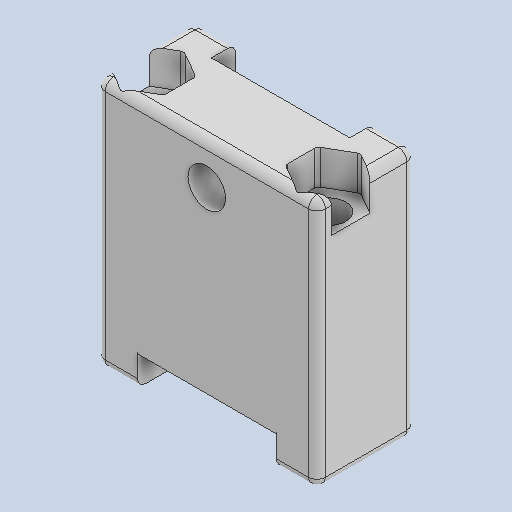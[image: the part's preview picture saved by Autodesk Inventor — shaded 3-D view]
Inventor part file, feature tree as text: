
AUTODESK INVENTOR PART (.ipt)
format: ipt  version: 2022 (Build 260153000, 153)  size: 158,208 bytes
history: native  units: in
note: dims shown in document units (in); Inventor stores cm internally (conversion verified against a paired STEP export)
features: fillet x1
ambient origin geometry x8: Origin, YZ Plane, XZ Plane, XY Plane, X Axis, Y Axis, Z Axis, Center Point
bodies: Solid1 (feature_tree)
feature tree (1):
  fillet  "Fillet2"  [1 undecoded]
note: 1 required parameter value undecoded (feature->parameter linkage not recoverable at this tier; creation-order binding heuristic only, values carry confidence <= 0.55)
